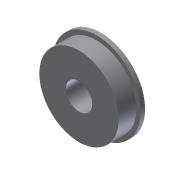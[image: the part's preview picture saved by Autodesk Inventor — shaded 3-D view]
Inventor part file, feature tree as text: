
AUTODESK INVENTOR PART (.ipt)
format: ipt  version: 2013 (Build 170138000, 138)  size: 90,112 bytes
history: native  units: in
note: dims shown in document units (in); Inventor stores cm internally (conversion verified against a paired STEP export)
features: extrude x2, sketch x2
ambient origin geometry x8: Origin, YZ Plane, XZ Plane, XY Plane, X Axis, Y Axis, Z Axis, Center Point
bodies: Solid1 (feature_tree)
feature tree (4):
  extrude  "Extrusion1"  Depth=1.125in
  extrude  "Extrusion2"  Depth=1.25in
  sketch  "Sketch1"  dims[d0=0.375in d1=1.125in]
  sketch  "Sketch2"  dims[d2=0.25in d3=0.0in d4=1.25in d5=0.062in d6=0.0in]
